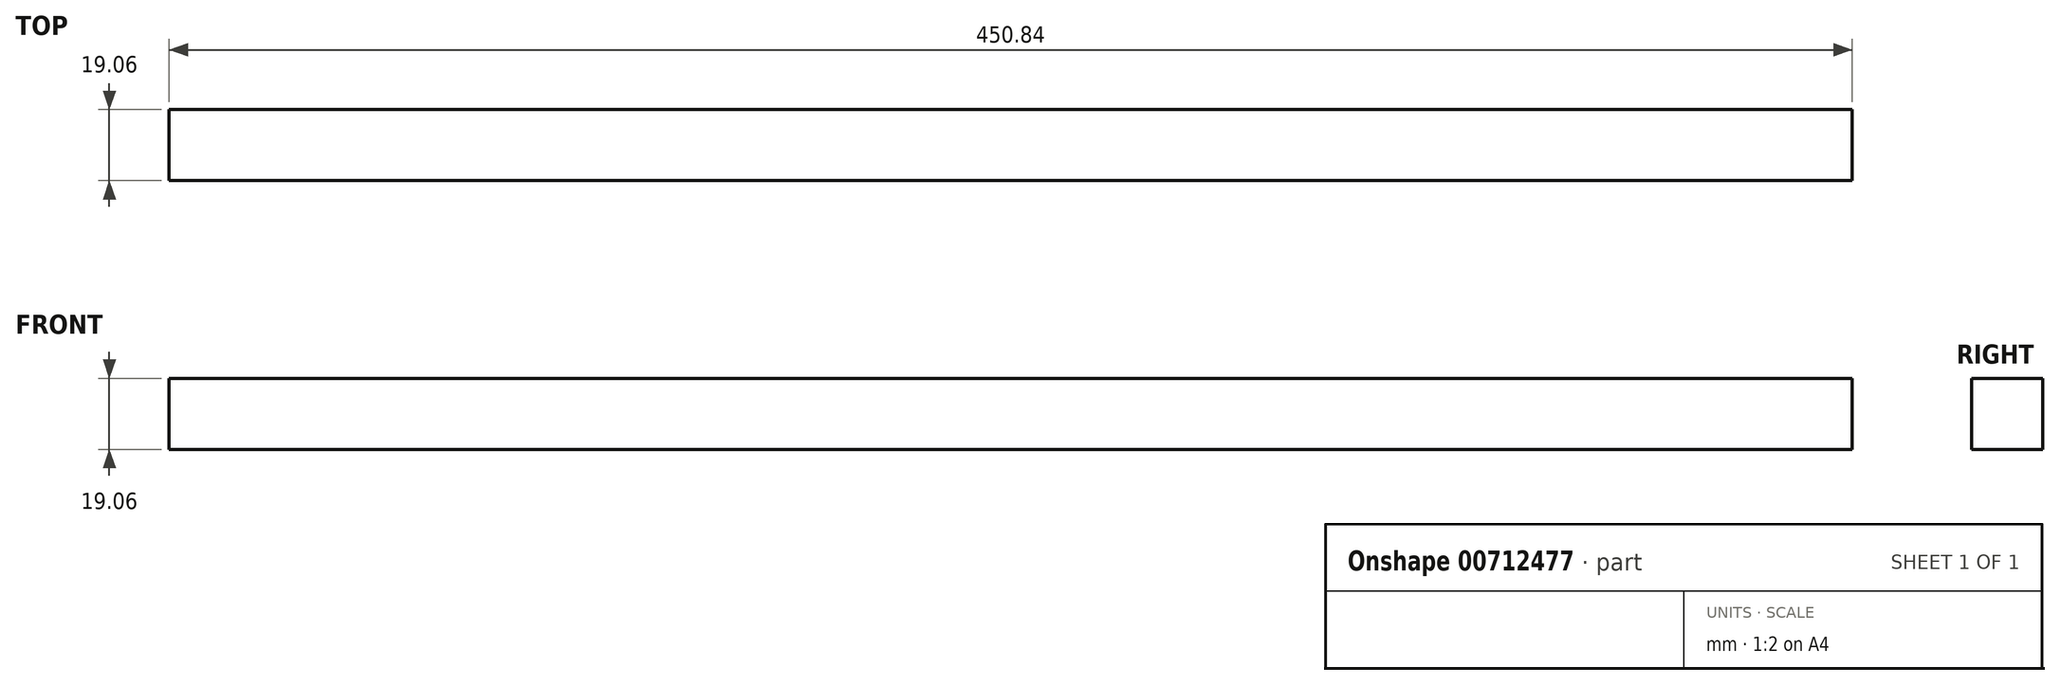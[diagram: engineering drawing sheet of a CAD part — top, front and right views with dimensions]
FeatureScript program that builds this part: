
annotation { "Feature Type Name" : "Feature", "Feature Type Description" : "" }
export const myFeature = defineFeature(function(context is Context, id is Id, definition is map)
    precondition{}
    {
        {
            var Q0;
            Q0=qCreatedBy(makeId("Right.planeOp"),FACE);
            var sketch = newSketch(context, id + "F0", { "sketchPlane" : qUnion([Q0])});
            skLineSegment(sketch, "E0.bottom", {"start": v(9.52, 9.53) * mm, "end": v(-9.53, 9.53) * mm});
            skLineSegment(sketch, "E0.top", {"start": v(9.53, -9.53) * mm, "end": v(-9.52, -9.53) * mm});
            skLineSegment(sketch, "E0.left", {"start": v(9.52, 9.53) * mm, "end": v(9.53, -9.53) * mm});
            skLineSegment(sketch, "E0.right", {"start": v(-9.53, 9.53) * mm, "end": v(-9.52, -9.53) * mm});
            skPoint(sketch, "E0.middle", {"position": v(0, 0) * mm});
            skSolve(sketch);
        }
        {
            var Q0;
            Q0 = qSketchRegion(id + "F0", true);
            extrude(context, id + "F1", {"entities" : qUnion([Q0]), "endBound" : BoundingType.SYMMETRIC, "depth" : 450.85 * mm, "offsetDistance" : 25.4 * mm});
        }
    });
